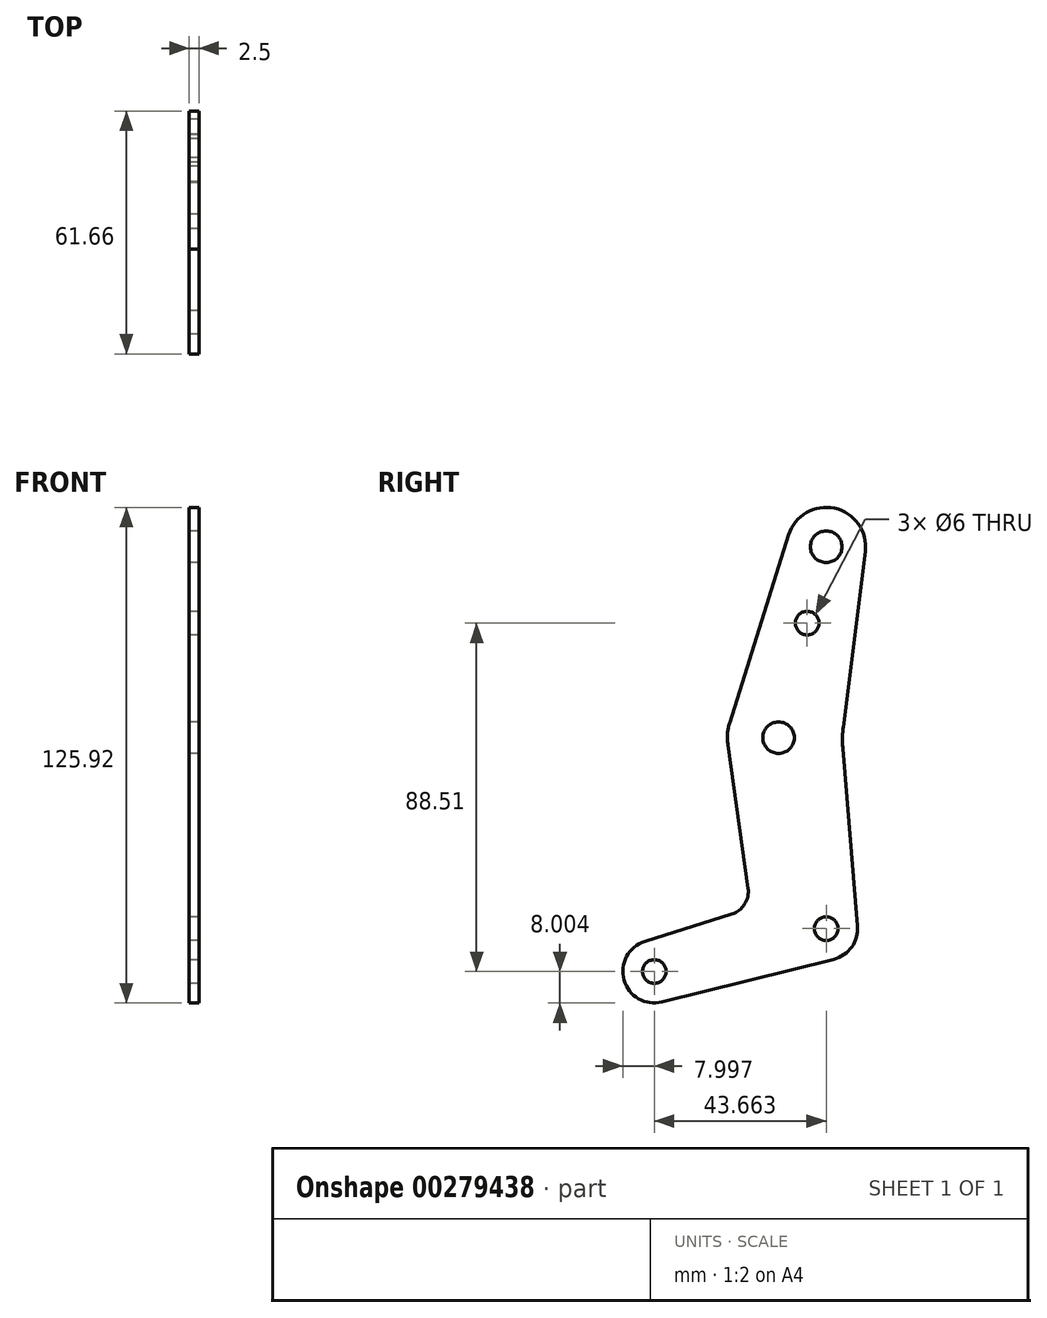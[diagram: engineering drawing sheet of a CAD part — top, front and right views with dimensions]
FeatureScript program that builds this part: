
annotation { "Feature Type Name" : "Feature", "Feature Type Description" : "" }
export const myFeature = defineFeature(function(context is Context, id is Id, definition is map)
    precondition{}
    {
        {
            var Q0;
            Q0=qCreatedBy(makeId("Right.planeOp"),FACE);
            var sketch = newSketch(context, id + "F0", { "sketchPlane" : qUnion([Q0])});
            skLineSegment(sketch, "E0", {"start": v(0, 0) * mm, "end": v(0, 97.03) * mm, "construction": true});
            skLineSegment(sketch, "E1", {"start": v(0, 0) * mm, "end": v(-12.1, 48.51) * mm, "construction": true});
            skLineSegment(sketch, "E2", {"start": v(-12.1, 48.51) * mm, "end": v(0, 97.03) * mm, "construction": true});
            skCircle(sketch, "E3", {"center": v(0, 0) * mm, "radius": 3 * mm});
            skCircle(sketch, "E4", {"center": v(-12.1, 48.51) * mm, "radius": 4 * mm});
            skCircle(sketch, "E5", {"center": v(0, 97.03) * mm, "radius": 4 * mm});
            skCircle(sketch, "E6", {"center": v(-4.84, 77.62) * mm, "radius": 3 * mm});
            skLineSegment(sketch, "E7", {"start": v(0, 0) * mm, "end": v(-43.66, -10.89) * mm, "construction": true});
            skCircle(sketch, "E8", {"center": v(-43.66, -10.89) * mm, "radius": 3 * mm});
            skArc(sketch, "E9", {"start": v(-46.06, -3.26) * mm, "mid": v(-51.36, -13.06) * mm, "end": v(-41.73, -18.65) * mm});
            skArc(sketch, "E10", {"start": v(1.94, -7.76) * mm, "mid": v(6.5, -4.66) * mm, "end": v(7.97, 0.66) * mm});
            skArc(sketch, "E11", {"start": v(9.92, 95.79) * mm, "mid": v(2.13, 106.8) * mm, "end": v(-9.54, 100.03) * mm});
            skLineSegment(sketch, "E12", {"start": v(-41.73, -18.65) * mm, "end": v(1.94, -7.76) * mm});
            skLineSegment(sketch, "E13", {"start": v(-46.06, -3.26) * mm, "end": v(-23.98, 3.7) * mm});
            skLineSegment(sketch, "E14", {"start": v(-19.84, 10.25) * mm, "end": v(-24.97, 46.7) * mm});
            skLineSegment(sketch, "E15", {"start": v(-24.5, 52.41) * mm, "end": v(-9.54, 100.03) * mm});
            skPoint(sketch, "E16.visualSharp", {"position": v(-19.13, 5.22) * mm});
            skArc(sketch, "E16.filletArc", {"start": v(-23.98, 3.7) * mm, "mid": v(-20.7, 6.21) * mm, "end": v(-19.84, 10.25) * mm});
            skArc(sketch, "E17.trimOffspring", {"start": v(-24.5, 52.41) * mm, "mid": v(-25.05, 49.58) * mm, "end": v(-24.97, 46.7) * mm});
            skPoint(sketch, "E18.orphan", {"position": v(0, -8.24) * mm});
            skLineSegment(sketch, "E19", {"start": v(9.92, 95.79) * mm, "end": v(4.34, 51.2) * mm});
            skPoint(sketch, "E19.endSnap0", {"position": v(0, 48.51) * mm});
            skLineSegment(sketch, "E20", {"start": v(4.23, 45.82) * mm, "end": v(8.03, 0) * mm});
            skPoint(sketch, "E21.visualSharp", {"position": v(4, 48.51) * mm});
            skArc(sketch, "E21.filletArc", {"start": v(4.34, 51.2) * mm, "mid": v(4.15, 48.51) * mm, "end": v(4.23, 45.82) * mm});
            skSolve(sketch);
        }
        {
            var Q0;
            Q0 = qSketchRegion(id + "F0", true);
            extrude(context, id + "F1", {"entities" : qUnion([Q0]), "depth" : 2.5 * mm});
        }
    });
